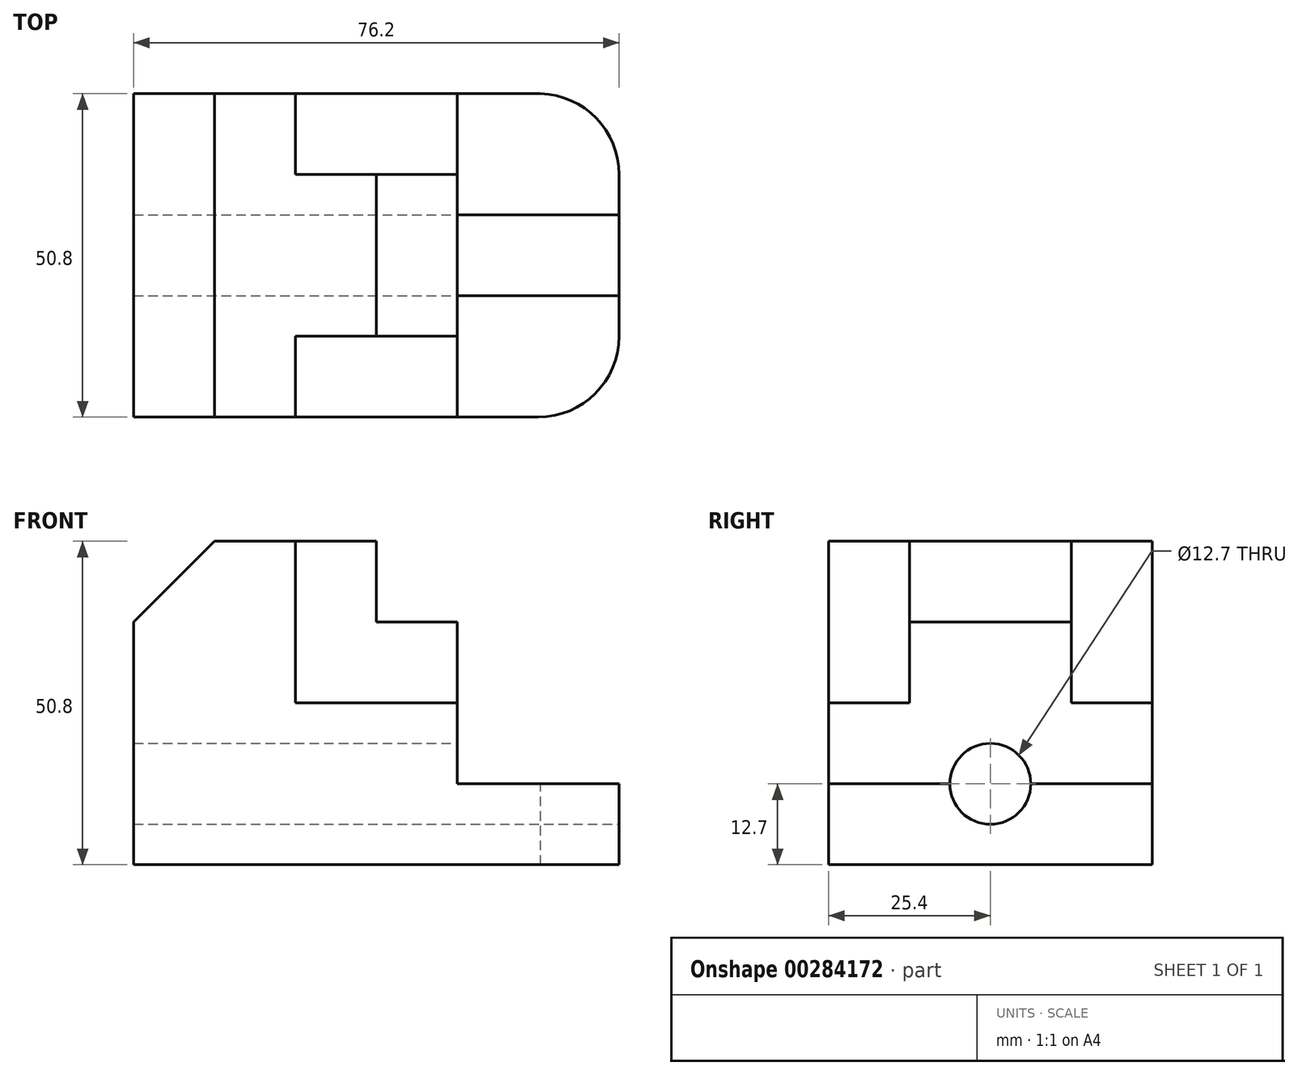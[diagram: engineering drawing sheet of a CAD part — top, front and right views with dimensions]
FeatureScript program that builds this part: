
annotation { "Feature Type Name" : "Feature", "Feature Type Description" : "" }
export const myFeature = defineFeature(function(context is Context, id is Id, definition is map)
    precondition{}
    {
        {
            var Q0;
            Q0=qCreatedBy(makeId("Front.planeOp"),FACE);
            var sketch = newSketch(context, id + "F0", { "sketchPlane" : qUnion([Q0])});
            skLineSegment(sketch, "E0", {"start": v(-76.2, -50.8) * mm, "end": v(-76.2, -12.7) * mm});
            skLineSegment(sketch, "E1", {"start": v(-76.2, -12.7) * mm, "end": v(-63.5, 0) * mm});
            skLineSegment(sketch, "E2", {"start": v(-38.1, 0) * mm, "end": v(-38.1, -12.7) * mm});
            skLineSegment(sketch, "E3", {"start": v(-38.1, -12.7) * mm, "end": v(-25.4, -12.7) * mm});
            skLineSegment(sketch, "E4", {"start": v(-25.4, -12.7) * mm, "end": v(-25.4, -38.1) * mm});
            skLineSegment(sketch, "E5", {"start": v(-25.4, -38.1) * mm, "end": v(0, -38.1) * mm});
            skLineSegment(sketch, "E6", {"start": v(0, -50.8) * mm, "end": v(-76.2, -50.8) * mm});
            skLineSegment(sketch, "E7", {"start": v(-63.5, 0) * mm, "end": v(-38.1, 0) * mm});
            skLineSegment(sketch, "E8", {"start": v(0, -38.1) * mm, "end": v(0, -50.8) * mm});
            skSolve(sketch);
        }
        {
            var Q0;
            Q0 = qSketchRegion(id + "F0", true);
            extrude(context, id + "F1", {"entities" : qUnion([Q0]), "endBound" : BoundingType.SYMMETRIC, "oppositeDirection" : true, "depth" : 50.8 * mm});
        }
        {
            var Q0;
            Q0=qCreatedBy(makeId("Right.planeOp"),FACE);
            var sketch = newSketch(context, id + "F2", { "sketchPlane" : qUnion([Q0])});
            skLineSegment(sketch, "E9.bottom", {"start": v(-25.4, -25.4) * mm, "end": v(-12.7, -25.4) * mm});
            skLineSegment(sketch, "E9.top", {"start": v(-25.4, 0) * mm, "end": v(-12.7, 0) * mm});
            skLineSegment(sketch, "E9.left", {"start": v(-25.4, -25.4) * mm, "end": v(-25.4, 0) * mm});
            skLineSegment(sketch, "E9.right", {"start": v(-12.7, -25.4) * mm, "end": v(-12.7, 0) * mm});
            skLineSegment(sketch, "E10.bottom", {"start": v(12.7, 0) * mm, "end": v(25.4, 0) * mm});
            skLineSegment(sketch, "E10.top", {"start": v(12.7, -25.4) * mm, "end": v(25.4, -25.4) * mm});
            skLineSegment(sketch, "E10.left", {"start": v(12.7, 0) * mm, "end": v(12.7, -25.4) * mm});
            skLineSegment(sketch, "E10.right", {"start": v(25.4, 0) * mm, "end": v(25.4, -25.4) * mm});
            skSolve(sketch);
        }
        {
            var Q0;
            Q0 = qSketchRegion(id + "F2", true);
            extrude(context, id + "F3", {"entities" : qUnion([Q0]), "operationType" : NewBodyOperationType.REMOVE, "oppositeDirection" : true, "depth" : 50.8 * mm});
        }
        {
            var Q0;
            Q0=qCreatedBy(makeId("Right.planeOp"),FACE);
            var sketch = newSketch(context, id + "F4", { "sketchPlane" : qUnion([Q0])});
            skCircle(sketch, "E11", {"center": v(0, -38.1) * mm, "radius": 6.35 * mm});
            skSolve(sketch);
        }
        {
            var Q0;
            Q0 = qSketchRegion(id + "F4", true);
            extrude(context, id + "F5", {"entities" : qUnion([Q0]), "operationType" : NewBodyOperationType.REMOVE, "endBound" : BoundingType.THROUGH_ALL, "oppositeDirection" : true, "depth" : 25.4 * mm});
        }
        {
            var Q0;
            Q0=qCreatedBy(makeId("Top.planeOp"),FACE);
            var sketch = newSketch(context, id + "F6", { "sketchPlane" : qUnion([Q0])});
            skArc(sketch, "E12", {"start": v(-12.7, -25.4) * mm, "mid": v(-3.72, -21.68) * mm, "end": v(0, -12.7) * mm});
            skLineSegment(sketch, "E13", {"start": v(-12.7, -25.4) * mm, "end": v(0, -25.4) * mm});
            skLineSegment(sketch, "E14", {"start": v(0, -25.4) * mm, "end": v(0, -12.7) * mm});
            skLineSegment(sketch, "E15", {"start": v(0, 12.7) * mm, "end": v(0, 25.4) * mm});
            skLineSegment(sketch, "E16", {"start": v(0, 25.4) * mm, "end": v(-12.7, 25.4) * mm});
            skArc(sketch, "E17", {"start": v(0, 12.7) * mm, "mid": v(-3.72, 21.69) * mm, "end": v(-12.7, 25.4) * mm});
            skSolve(sketch);
        }
        {
            var Q0;
            Q0 = qSketchRegion(id + "F6", true);
            extrude(context, id + "F7", {"entities" : qUnion([Q0]), "operationType" : NewBodyOperationType.REMOVE, "endBound" : BoundingType.THROUGH_ALL, "oppositeDirection" : true, "depth" : 25.4 * mm});
        }
    });
